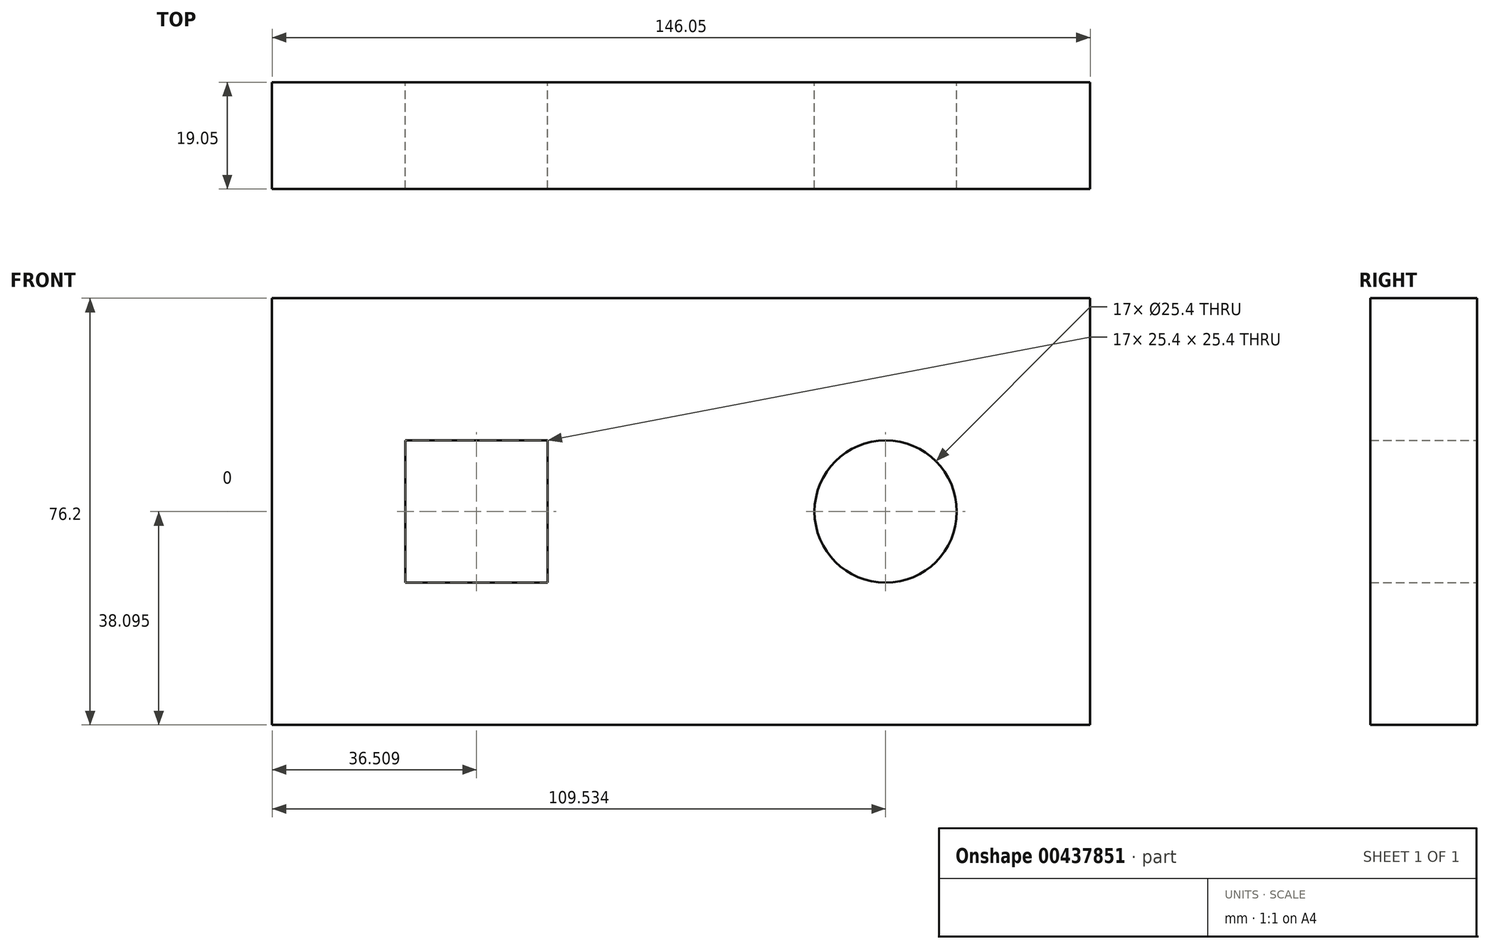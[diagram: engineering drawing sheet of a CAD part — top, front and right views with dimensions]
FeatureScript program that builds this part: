
annotation { "Feature Type Name" : "Feature", "Feature Type Description" : "" }
export const myFeature = defineFeature(function(context is Context, id is Id, definition is map)
    precondition{}
    {
        {
            var Q0;
            Q0=qCreatedBy(makeId("Front.planeOp"),FACE);
            var sketch = newSketch(context, id + "F0", { "sketchPlane" : qUnion([Q0])});
            skLineSegment(sketch, "E0.bottom", {"start": v(-74.82, 45.27) * mm, "end": v(71.23, 45.27) * mm});
            skLineSegment(sketch, "E0.top", {"start": v(-74.82, -30.93) * mm, "end": v(71.23, -30.93) * mm});
            skLineSegment(sketch, "E0.left", {"start": v(-74.82, 45.27) * mm, "end": v(-74.82, -30.93) * mm});
            skLineSegment(sketch, "E0.right", {"start": v(71.23, 45.27) * mm, "end": v(71.23, -30.93) * mm});
            skCircle(sketch, "E1", {"center": v(34.71, 7.17) * mm, "radius": 12.7 * mm});
            skLineSegment(sketch, "E2.bottom", {"start": v(-51.01, 19.87) * mm, "end": v(-25.61, 19.87) * mm});
            skLineSegment(sketch, "E2.top", {"start": v(-51.01, -5.53) * mm, "end": v(-25.61, -5.53) * mm});
            skLineSegment(sketch, "E2.left", {"start": v(-51.01, 19.87) * mm, "end": v(-51.01, -5.53) * mm});
            skLineSegment(sketch, "E2.right", {"start": v(-25.61, 19.87) * mm, "end": v(-25.61, -5.53) * mm});
            skSolve(sketch);
        }
        {
            var Q0;
            Q0 = qSketchRegion(id + "F0", true);
            extrude(context, id + "F1", {"entities" : qUnion([Q0]), "depth" : 19.05 * mm});
        }
    });
